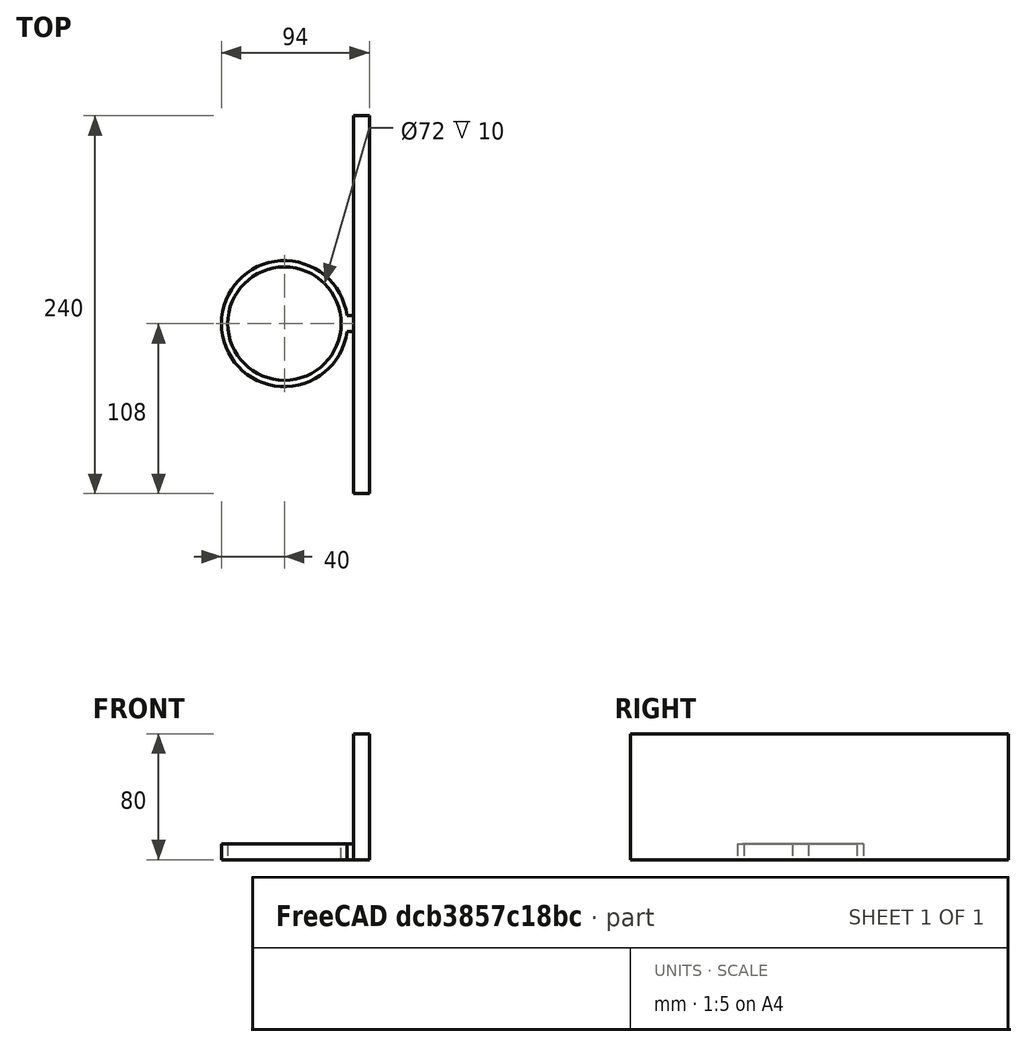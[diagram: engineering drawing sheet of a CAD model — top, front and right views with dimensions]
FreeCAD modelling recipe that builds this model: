
FCSTD DOCUMENT  (FreeCAD 0.20R29177 +233 (Git))
Label: movil_holder
License: Creative Commons Attribution-ShareAlike
LicenseURL: http://creativecommons.org/licenses/by-sa/4.0/
objects: Part::Cylinder×2, Part::Box×2, Part::Cut×1, Part::MultiFuse×1
note: 6 computed .brp shape members not serialized (recipe doc carries the construction recipe); baked Part::Feature solids carry a one-line shape summary decoded from their .brp

FEATURE [Part::Cylinder] Cylinder
  Angle = 360
  AttacherType = Attacher::AttachEngine3D
  FirstAngle = 0
  Height = 10
  Radius = 40
  SecondAngle = 0
FEATURE [Part::Cylinder] Cylinder001
  Angle = 360
  AttacherType = Attacher::AttachEngine3D
  FirstAngle = 0
  Height = 10
  Radius = 36
  SecondAngle = 0
FEATURE [Part::Cut] Cut
  Base = -> Cylinder
  Refine = true
  Tool = -> Cylinder001
FEATURE [Part::Box] Box  label="Cube"
  AttacherType = Attacher::AttachEngine3D
  Height = 10
  Length = 10
  Placement = pos=(38,-5,0) rot=(0,0,1;0rad)
  Width = 10
FEATURE [Part::Box] Box001  label="Cube001"
  AttacherType = Attacher::AttachEngine3D
  Height = 80
  Length = 10
  Placement = pos=(44,-108,0) rot=(0,0,1;0rad)
  Width = 240
FEATURE [Part::MultiFuse] Fusion
  Refine = true
  Shapes = -> [Cut,Box,Box001]
